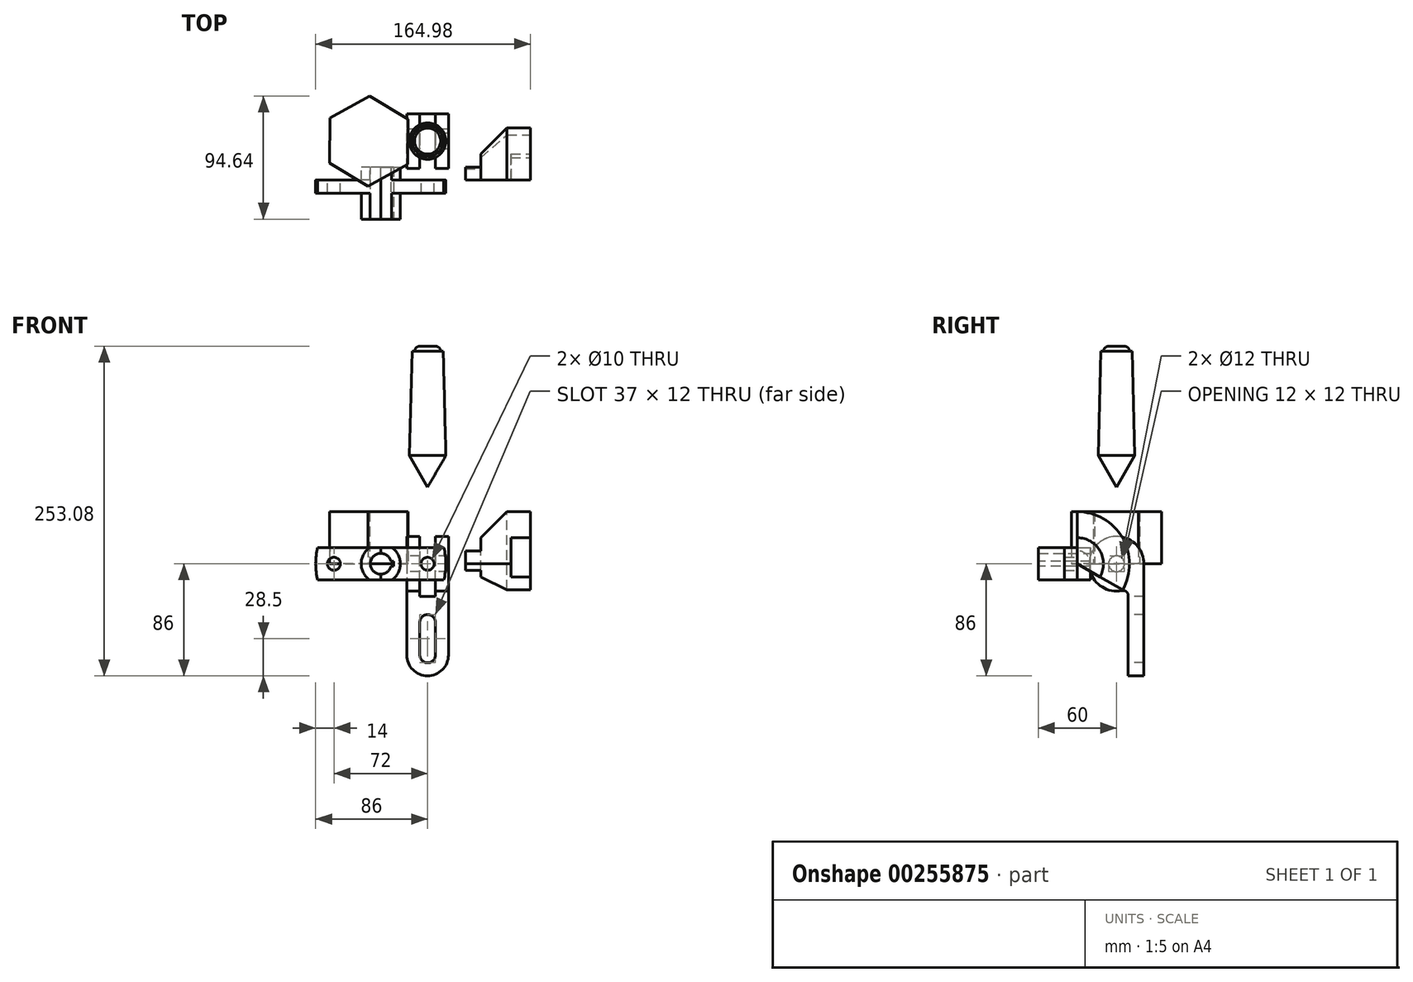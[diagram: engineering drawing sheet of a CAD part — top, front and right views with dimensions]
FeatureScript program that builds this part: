
annotation { "Feature Type Name" : "Feature", "Feature Type Description" : "" }
export const myFeature = defineFeature(function(context is Context, id is Id, definition is map)
    precondition{}
    {
        {
            var Q0;
            Q0=qCreatedBy(makeId("Right.planeOp"),FACE);
            var sketch = newSketch(context, id + "F0", { "sketchPlane" : qUnion([Q0])});
            skArc(sketch, "E0", {"start": v(21, 0) * mm, "mid": v(-16.27, 13.28) * mm, "end": v(4.2, -20.58) * mm});
            skLineSegment(sketch, "E1.top", {"start": v(9, -86) * mm, "end": v(21, -86) * mm});
            skLineSegment(sketch, "E1.left", {"start": v(9, -24.5) * mm, "end": v(9, -86) * mm});
            skLineSegment(sketch, "E1.right", {"start": v(21, 0) * mm, "end": v(21, -86) * mm});
            skCircle(sketch, "E2", {"center": v(0, 0) * mm, "radius": 6 * mm});
            skPoint(sketch, "E3.visualSharp", {"position": v(9, -18.97) * mm});
            skArc(sketch, "E3.filletArc", {"start": v(9, -24.5) * mm, "mid": v(7.53, -21.4) * mm, "end": v(4.2, -20.58) * mm});
            skSolve(sketch);
        }
        {
            var Q0;
            Q0=makeQuery(id+"F0.imprint","IMPRINT",FACE,{"disambiguationData":[TD([[makeQuery(id+"F0.imprint","IMPRINT",EDGE,{"derivedFrom":sQuery(id+"F0.wireOp",EDGE,"E0")}),1.0]])]});
            extrude(context, id + "F1", {"entities" : qUnion([Q0]), "endBound" : BoundingType.SYMMETRIC, "depth" : 32 * mm});
        }
        {
            var Q0;
            Q0=qCreatedBy(makeId("Front.planeOp"),FACE);
            cPlane(context, id + "F2", {"entities" : qUnion([Q0]), "cplaneType" : CPlaneType.OFFSET, "offset" : 30 * mm, "width" : 150 * mm, "height" : 150 * mm});
        }
        {
            var Q0;
            Q0=qCreatedBy(id+"F2.planeOp",FACE);
            var sketch = newSketch(context, id + "F3", { "sketchPlane" : qUnion([Q0])});
            skLineSegment(sketch, "E4.bottom", {"start": v(-6, 21) * mm, "end": v(6, 21) * mm});
            skLineSegment(sketch, "E4.top", {"start": v(-6, -25) * mm, "end": v(6, -25) * mm});
            skLineSegment(sketch, "E4.left", {"start": v(-6, 21) * mm, "end": v(-6, -25) * mm});
            skLineSegment(sketch, "E4.right", {"start": v(6, 21) * mm, "end": v(6, -25) * mm});
            skLineSegment(sketch, "E5.left", {"start": v(-6, -45) * mm, "end": v(-6, -70) * mm});
            skLineSegment(sketch, "E5.right", {"start": v(6, -45) * mm, "end": v(6, -70) * mm});
            skLineSegment(sketch, "E6", {"start": v(-16, 21) * mm, "end": v(16, 21) * mm});
            skLineSegment(sketch, "E7.0", {"start": v(-16, -24.5) * mm, "end": v(-16, -86) * mm});
            skLineSegment(sketch, "E8.0", {"start": v(16, -24.5) * mm, "end": v(16, -86) * mm});
            skLineSegment(sketch, "E9.0", {"start": v(16, -86) * mm, "end": v(-16, -86) * mm});
            skArc(sketch, "E10", {"start": v(-6, -45) * mm, "mid": v(0, -39) * mm, "end": v(6, -45) * mm});
            skArc(sketch, "E11", {"start": v(6, -70) * mm, "mid": v(0, -76) * mm, "end": v(-6, -70) * mm});
            skArc(sketch, "E12", {"start": v(-16, -70) * mm, "mid": v(0, -86) * mm, "end": v(16, -70) * mm});
            skSolve(sketch);
        }
        {
            var Q0;
            Q0=makeQuery(id+"F3.imprint","IMPRINT",FACE,{"disambiguationData":[TD([[makeQuery(id+"F3.imprint","IMPRINT",EDGE,{"derivedFrom":sQuery(id+"F3.wireOp",EDGE,"E4.top")}),1.0]])]});
            var Q1;
            Q1=makeQuery(id+"F3.imprint","IMPRINT",FACE,{"disambiguationData":[TD([[makeQuery(id+"F3.imprint","IMPRINT",EDGE,{"derivedFrom":sQuery(id+"F3.wireOp",EDGE,"E5.left")}),1.0]])]});
            var Q2;
            {var subQ0=sQuery(id+"F3.wireOp",EDGE,"E9.0");var subQ1=sQuery(id+"F3.wireOp",EDGE,"E7.0");var subQ2=makeQuery(id+"F3.imprint","INTERSECT",VERTEX,{"derivedFrom":[subQ1,subQ0]});Q2=makeQuery(id+"F3.imprint","IMPRINT",FACE,{"disambiguationData":[TD([[makeQuery(id+"F3.imprint","IMPRINT",EDGE,{"disambiguationData":[TD([[subQ2,1.0]])],"derivedFrom":subQ1}),1.0]])]});}
            var Q3;
            {var subQ0=sQuery(id+"F3.wireOp",EDGE,"E9.0");var subQ1=sQuery(id+"F3.wireOp",EDGE,"E8.0");var subQ2=makeQuery(id+"F3.imprint","INTERSECT",VERTEX,{"derivedFrom":[subQ1,subQ0]});Q3=makeQuery(id+"F3.imprint","IMPRINT",FACE,{"disambiguationData":[TD([[makeQuery(id+"F3.imprint","IMPRINT",EDGE,{"disambiguationData":[TD([[subQ2,1.0]])],"derivedFrom":subQ1}),-1.0]])]});}
            extrude(context, id + "F4", {"entities" : qUnion([Q0, Q1, Q2, Q3]), "operationType" : NewBodyOperationType.REMOVE, "endBound" : BoundingType.THROUGH_ALL, "oppositeDirection" : true, "depth" : 25 * mm});
        }
        {
            var Q0;
            Q0=qCreatedBy(id+"F2.planeOp",FACE);
            var sketch = newSketch(context, id + "F5", { "sketchPlane" : qUnion([Q0])});
            skArc(sketch, "E13", {"start": v(-36, -8) * mm, "mid": v(-28, 0) * mm, "end": v(-36, 8) * mm});
            skArc(sketch, "E14", {"start": v(12.41, -12.5) * mm, "mid": v(14, 0) * mm, "end": v(12.41, 12.5) * mm});
            skLineSegment(sketch, "E15", {"start": v(-36, 12.5) * mm, "end": v(-27.7, 12.5) * mm});
            skLineSegment(sketch, "E16", {"start": v(-36, -12.5) * mm, "end": v(-27.7, -12.5) * mm});
            skCircle(sketch, "E17", {"center": v(0, 0) * mm, "radius": 5 * mm});
            skLineSegment(sketch, "E18", {"start": v(-27.7, 12.5) * mm, "end": v(12.41, 12.5) * mm});
            skLineSegment(sketch, "E19", {"start": v(-27.7, -12.5) * mm, "end": v(12.41, -12.5) * mm});
            skArc(sketch, "E20.trimOffspring", {"start": v(-27.7, -12.5) * mm, "mid": v(-21, 0) * mm, "end": v(-27.7, 12.5) * mm});
            skLineSegment(sketch, "E21", {"start": v(-36, 12.5) * mm, "end": v(-36, -12.5) * mm});
            skPoint(sketch, "E22.start.orphan", {"position": v(-44.3, 12.5) * mm});
            skPoint(sketch, "E23.orphan", {"position": v(-44.3, -12.5) * mm});
            skSolve(sketch);
        }
        {
            var Q0;
            {var subQ2=sQuery(id+"F5.wireOp",EDGE,"E13");Q0=makeQuery(id+"F5.imprint","IMPRINT",FACE,{"disambiguationData":[TD([[makeQuery(id+"F5.imprint","IMPRINT",EDGE,{"derivedFrom":subQ2}),-1.0]])]});}
            extrude(context, id + "F6", {"entities" : qUnion([Q0]), "depth" : 30 * mm, "hasSecondDirection" : true, "secondDirectionOppositeDirection" : true, "secondDirectionDepth" : 10 * mm});
        }
        {
            var Q0;
            Q0=makeQuery(id+"F5.imprint","IMPRINT",FACE,{"disambiguationData":[TD([[makeQuery(id+"F5.imprint","IMPRINT",EDGE,{"derivedFrom":sQuery(id+"F5.wireOp",EDGE,"E14")}),1.0]])]});
            extrude(context, id + "F7", {"entities" : qUnion([Q0]), "operationType" : NewBodyOperationType.ADD, "depth" : 10 * mm});
        }
        {
            var Q0;
            {var subQ0=sQuery(id+"F5.wireOp",EDGE,"E21");Q0=makeQuery(id+"F6.opExtrude","SWEPT_FACE",FACE,{"disambiguationData":[OSD([subQ0]),TDD([makeQuery(id+"F5.imprint","IMPRINT",EDGE,{"disambiguationData":[TD([[makeQuery(id+"F5.imprint","INTERSECT",VERTEX,{"disambiguationData":[OD(1.0)],"derivedFrom":[sQuery(id+"F5.wireOp",EDGE,"E13"),subQ0]}),1.0]])],"derivedFrom":subQ0})])]});}
            cPlane(context, id + "F8", {"entities" : qUnion([Q0]), "cplaneType" : CPlaneType.OFFSET, "offset" : 0 * mm, "width" : 150 * mm, "height" : 150 * mm});
        }
        {
            var Q0;
            Q0=makeQuery(id+"F6.opExtrude","SWEPT_BODY",BODY,{"disambiguationData":[OSD([sQuery(id+"F5.wireOp",EDGE,"E13"),sQuery(id+"F5.wireOp",EDGE,"E15"),sQuery(id+"F5.wireOp",EDGE,"E16"),sQuery(id+"F5.wireOp",EDGE,"E20.trimOffspring"),sQuery(id+"F5.wireOp",EDGE,"E21")])]});
            var Q1;
            Q1=qCreatedBy(id+"F8.planeOp",FACE);
            mirror(context, id + "F9", {"operationType" : NewBodyOperationType.ADD, "entities" : qUnion([Q0]), "mirrorPlane" : qUnion([Q1])});
        }
        {
            var Q0;
            {var subQ0=makeQuery(id+"F6.opExtrude","CAP_FACE",FACE,{"disambiguationData":[OSD([sQuery(id+"F5.wireOp",EDGE,"E13"),sQuery(id+"F5.wireOp",EDGE,"E15"),sQuery(id+"F5.wireOp",EDGE,"E16"),sQuery(id+"F5.wireOp",EDGE,"E20.trimOffspring"),sQuery(id+"F5.wireOp",EDGE,"E21")])],"isStart":false});Q0=makeQuery(id+"F9.boolean.opBoolean","MERGE",FACE,{"derivedFrom":[subQ0,makeQuery(id+"F9.opPattern","COPY",FACE,{"derivedFrom":subQ0,"instanceName":"1"})]});}
            var sketch = newSketch(context, id + "F10", { "sketchPlane" : qUnion([Q0])});
            skLineSegment(sketch, "E24.bottom", {"start": v(-26, -2) * mm, "end": v(-32.04, -2) * mm});
            skLineSegment(sketch, "E24.top", {"start": v(-26, 2) * mm, "end": v(-32.04, 2) * mm});
            skLineSegment(sketch, "E24.left", {"start": v(-26, -2) * mm, "end": v(-26, 2) * mm});
            skLineSegment(sketch, "E24.right", {"start": v(-32.04, -2) * mm, "end": v(-32.04, 2) * mm});
            skPoint(sketch, "E24.middle", {"position": v(-29.02, 0) * mm});
            skPoint(sketch, "E25", {"position": v(-44, 0) * mm});
            skSolve(sketch);
        }
        {
            var Q0;
            {var subQ0=sQuery(id+"F10.wireOp",EDGE,"E24.left");Q0=makeQuery(id+"F10.imprint","IMPRINT",FACE,{"disambiguationData":[TD([[makeQuery(id+"F10.imprint","IMPRINT",EDGE,{"derivedFrom":subQ0}),1.0]])]});}
            extrude(context, id + "F11", {"entities" : qUnion([Q0]), "operationType" : NewBodyOperationType.REMOVE, "endBound" : BoundingType.THROUGH_ALL, "oppositeDirection" : true, "depth" : 25 * mm});
        }
        {
            var Q0;
            Q0=qCreatedBy(makeId("Front.planeOp"),FACE);
            var sketch = newSketch(context, id + "F12", { "sketchPlane" : qUnion([Q0])});
            skLineSegment(sketch, "E26", {"start": v(0, 58.84) * mm, "end": v(14, 83.08) * mm});
            skLineSegment(sketch, "E27", {"start": v(14, 83.08) * mm, "end": v(12, 163.08) * mm});
            skLineSegment(sketch, "E28", {"start": v(12, 163.08) * mm, "end": v(10, 163.08) * mm});
            skLineSegment(sketch, "E29", {"start": v(10, 163.08) * mm, "end": v(10, 163.08) * mm});
            skLineSegment(sketch, "E30", {"start": v(6, 167.08) * mm, "end": v(0, 167.08) * mm});
            skLineSegment(sketch, "E31", {"start": v(0, 167.08) * mm, "end": v(0, 58.84) * mm});
            skPoint(sketch, "E32.visualSharp", {"position": v(10, 167.08) * mm});
            skArc(sketch, "E32.filletArc", {"start": v(10, 163.08) * mm, "mid": v(8.83, 165.91) * mm, "end": v(6, 167.08) * mm});
            skLineSegment(sketch, "E33", {"start": v(14, 83.08) * mm, "end": v(0, 83.08) * mm});
            skSolve(sketch);
        }
        {
            var Q0;
            {var subQ0=sQuery(id+"F12.wireOp",EDGE,"E26");Q0=makeQuery(id+"F12.imprint","IMPRINT",FACE,{"disambiguationData":[TD([[makeQuery(id+"F12.imprint","IMPRINT",EDGE,{"derivedFrom":subQ0}),1.0]])]});}
            var Q1;
            Q1=makeQuery(id+"F12.imprint","IMPRINT",FACE,{"disambiguationData":[TD([[makeQuery(id+"F12.imprint","IMPRINT",EDGE,{"derivedFrom":sQuery(id+"F12.wireOp",EDGE,"E27")}),1.0]])]});
            var Q2;
            Q2=sQuery(id+"F12.wireOp",EDGE,"E31");
            revolve(context, id + "F13", {"entities" : qUnion([Q0, Q1]), "axis" : qUnion([Q2]), "revolveType" : RevolveType.FULL});
        }
        {
            var Q0;
            Q0=qCreatedBy(id+"F2.planeOp",FACE);
            var sketch = newSketch(context, id + "F14", { "sketchPlane" : qUnion([Q0])});
            skLineSegment(sketch, "E34", {"start": v(63.98, 0) * mm, "end": v(28.98, 0) * mm});
            skLineSegment(sketch, "E35", {"start": v(28.98, 0) * mm, "end": v(28.98, 10) * mm});
            skLineSegment(sketch, "E36", {"start": v(28.98, 10) * mm, "end": v(40.98, 10) * mm});
            skLineSegment(sketch, "E37", {"start": v(40.98, 10) * mm, "end": v(40.98, 20) * mm});
            skLineSegment(sketch, "E38", {"start": v(40.98, 20) * mm, "end": v(60.98, 40) * mm});
            skLineSegment(sketch, "E39", {"start": v(60.98, 40) * mm, "end": v(78.98, 40) * mm});
            skLineSegment(sketch, "E40", {"start": v(78.98, 40) * mm, "end": v(78.98, 20) * mm});
            skPoint(sketch, "E41.end.orphan", {"position": v(63.98, 10) * mm});
            skLineSegment(sketch, "E42", {"start": v(63.98, 0) * mm, "end": v(63.98, 20) * mm});
            skLineSegment(sketch, "E43", {"start": v(63.98, 20) * mm, "end": v(78.98, 20) * mm});
            skPoint(sketch, "E44.orphan", {"position": v(78.98, 10) * mm});
            skSolve(sketch);
        }
        {
            var Q0;
            Q0=makeQuery(id+"F14.imprint","IMPRINT",FACE,{"disambiguationData":[TD([[makeQuery(id+"F14.imprint","IMPRINT",EDGE,{"derivedFrom":sQuery(id+"F14.wireOp",EDGE,"E34")}),-1.0]])]});
            var Q1;
            Q1=sQuery(id+"F14.wireOp",EDGE,"E34");
            revolve(context, id + "F15", {"entities" : qUnion([Q0]), "axis" : qUnion([Q1]), "revolveType" : RevolveType.ONE_DIRECTION, "angle" : 120 * degree});
        }
        {
            var Q0;
            Q0=qCreatedBy(makeId("Top.planeOp"),FACE);
            var sketch = newSketch(context, id + "F16", { "sketchPlane" : qUnion([Q0])});
            skCircle(sketch, "E45.cCircle", {"center": v(-45.18, 0) * mm, "radius": 30 * mm, "construction": true});
            skLineSegment(sketch, "E45.0", {"start": v(-44.6, 34.64) * mm, "end": v(-14.9, 16.81) * mm});
            skLineSegment(sketch, "E45.1", {"start": v(-14.9, 16.81) * mm, "end": v(-15.47, -17.82) * mm});
            skLineSegment(sketch, "E45.2", {"start": v(-15.47, -17.82) * mm, "end": v(-45.76, -34.64) * mm});
            skLineSegment(sketch, "E45.3", {"start": v(-45.76, -34.64) * mm, "end": v(-75.47, -16.81) * mm});
            skLineSegment(sketch, "E45.4", {"start": v(-75.47, -16.81) * mm, "end": v(-74.88, 17.82) * mm});
            skLineSegment(sketch, "E45.5", {"start": v(-74.88, 17.82) * mm, "end": v(-44.6, 34.64) * mm});
            skPoint(sketch, "E45.0.midPoint", {"position": v(-29.74, 25.72) * mm});
            skCircle(sketch, "E46", {"center": v(-45.18, 0) * mm, "radius": 30 * mm});
            skSolve(sketch);
        }
        {
            var Q0;
            Q0 = qSketchRegion(id + "F16", true);
            extrude(context, id + "F17", {"entities" : qUnion([Q0]), "depth" : 40 * mm});
        }
    });
